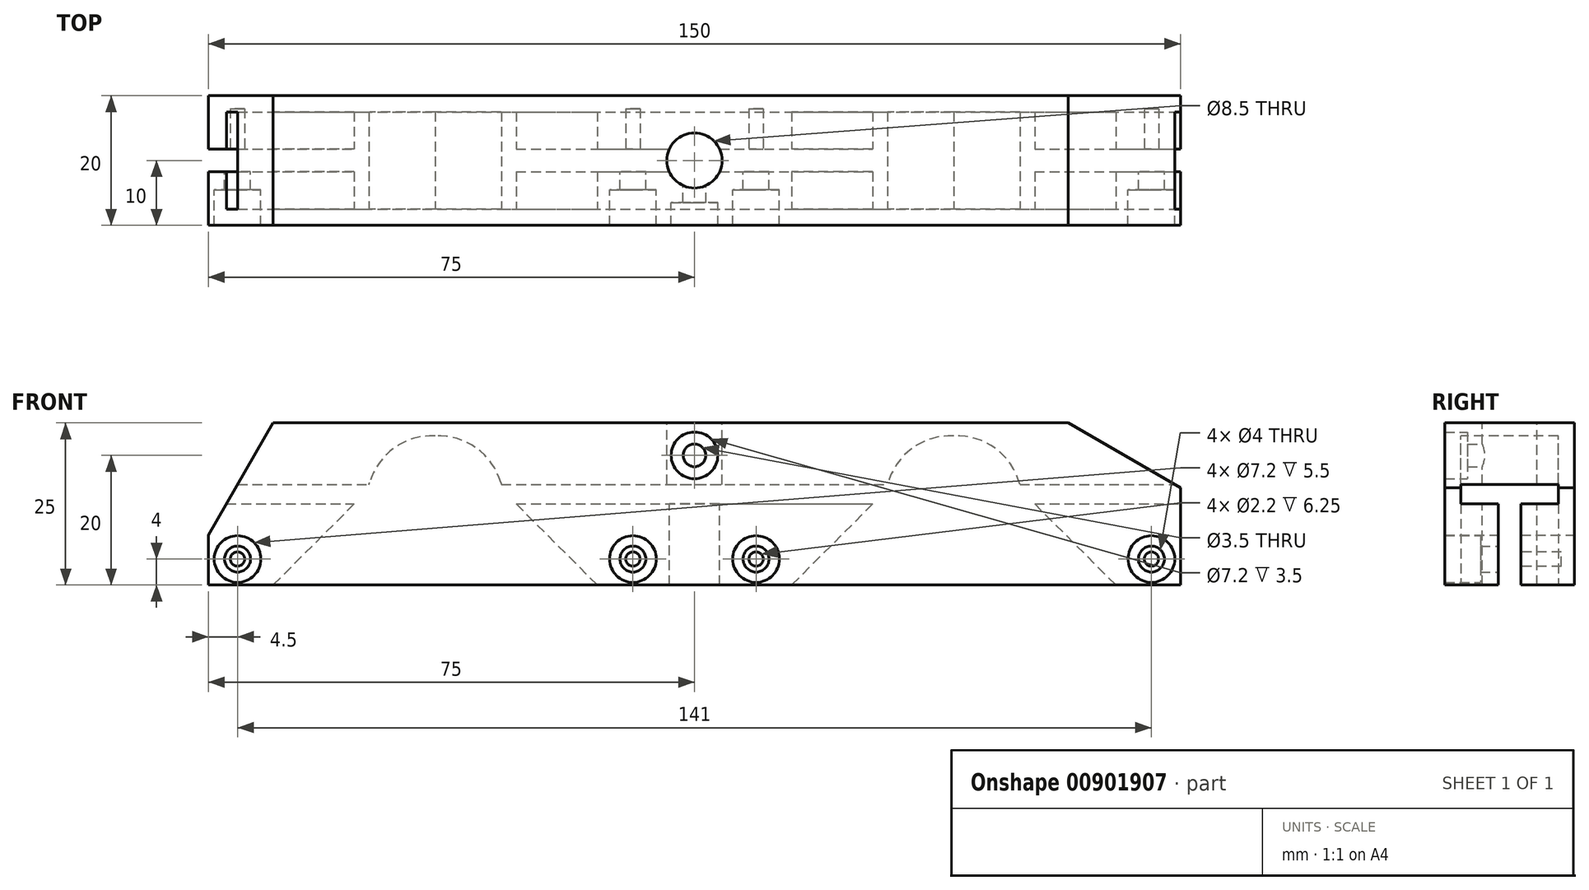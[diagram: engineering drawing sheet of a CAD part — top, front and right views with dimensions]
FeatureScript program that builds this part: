
annotation { "Feature Type Name" : "Feature", "Feature Type Description" : "" }
export const myFeature = defineFeature(function(context is Context, id is Id, definition is map)
    precondition{}
    {
        {
            var Q0;
            Q0=qCreatedBy(makeId("Front.planeOp"),FACE);
            var sketch = newSketch(context, id + "F0", { "sketchPlane" : qUnion([Q0])});
            skLineSegment(sketch, "E0.bottom", {"start": v(-75, 12.5) * mm, "end": v(75, 12.5) * mm});
            skLineSegment(sketch, "E0.top", {"start": v(-75, -12.5) * mm, "end": v(75, -12.5) * mm});
            skLineSegment(sketch, "E1", {"start": v(-50.5, -12.5) * mm, "end": v(-75, -12.5) * mm});
            skPoint(sketch, "E2.orphan", {"position": v(-50, 12.5) * mm});
            skPoint(sketch, "E3.orphan", {"position": v(50, 12.5) * mm});
            skLineSegment(sketch, "E4", {"start": v(-75, 12.5) * mm, "end": v(-75, -12.5) * mm});
            skLineSegment(sketch, "E5", {"start": v(75, 12.5) * mm, "end": v(75, -12.5) * mm});
            skSolve(sketch);
        }
        {
            var Q0;
            Q0=makeQuery(id+"F0.imprint","IMPRINT",FACE,{"disambiguationData":[TD([[makeQuery(id+"F0.imprint","IMPRINT",EDGE,{"derivedFrom":sQuery(id+"F0.wireOp",EDGE,"E0.bottom")}),-1.0]])]});
            extrude(context, id + "F1", {"entities" : qUnion([Q0]), "oppositeDirection" : true, "depth" : 10 * mm, "offsetDistance" : 25 * mm});
        }
        {
            var Q0;
            Q0=makeQuery(id+"F0.imprint","IMPRINT",FACE,{"disambiguationData":[TD([[makeQuery(id+"F0.imprint","IMPRINT",EDGE,{"derivedFrom":sQuery(id+"F0.wireOp",EDGE,"E0.bottom")}),-1.0]])]});
            var sketch = newSketch(context, id + "F2", { "sketchPlane" : qUnion([Q0])});
            skLineSegment(sketch, "E6", {"start": v(-40, 24.55) * mm, "end": v(-40, -25.43) * mm, "construction": true});
            skLineSegment(sketch, "E7", {"start": v(40, 21.57) * mm, "end": v(40, -24.69) * mm, "construction": true});
            skLineSegment(sketch, "E8", {"start": v(-41.62, 10.5) * mm, "end": v(42.45, 10.5) * mm, "construction": true});
            skLineSegment(sketch, "E9", {"start": v(-59.41, -12.5) * mm, "end": v(19.88, -12.5) * mm});
            skArc(sketch, "E10", {"start": v(-40, 10.5) * mm, "mid": v(-47.58, 7.58) * mm, "end": v(-50.5, 0) * mm});
            skArc(sketch, "E11", {"start": v(-29.5, 0) * mm, "mid": v(-32.42, 7.58) * mm, "end": v(-40, 10.5) * mm});
            skLineSegment(sketch, "E12", {"start": v(-50.5, 0) * mm, "end": v(-50.5, -12.5) * mm});
            skLineSegment(sketch, "E13", {"start": v(-29.5, 0) * mm, "end": v(-29.5, -12.5) * mm});
            skLineSegment(sketch, "E14", {"start": v(-29.5, 0) * mm, "end": v(17, 0) * mm});
            skArc(sketch, "E15", {"start": v(40, 10.5) * mm, "mid": v(32.42, 7.58) * mm, "end": v(29.5, 0) * mm});
            skArc(sketch, "E16", {"start": v(50.5, 0) * mm, "mid": v(47.58, 7.58) * mm, "end": v(40, 10.5) * mm});
            skLineSegment(sketch, "E17", {"start": v(17, -12.5) * mm, "end": v(62.5, -12.5) * mm});
            skLineSegment(sketch, "E18", {"start": v(17, 0) * mm, "end": v(29.5, 0) * mm});
            skLineSegment(sketch, "E19", {"start": v(62.5, -10.83) * mm, "end": v(62.5, -12.5) * mm});
            skLineSegment(sketch, "E20", {"start": v(50.5, 0) * mm, "end": v(52.5, 0) * mm});
            skLineSegment(sketch, "E21", {"start": v(62.5, -10) * mm, "end": v(62.5, -10.83) * mm});
            skLineSegment(sketch, "E22", {"start": v(29.5, 0) * mm, "end": v(29.5, -12.5) * mm});
            skLineSegment(sketch, "E23", {"start": v(50.5, 0) * mm, "end": v(50.5, -12.5) * mm});
            skPoint(sketch, "E24.orphan", {"position": v(-13.91, 0) * mm});
            skPoint(sketch, "E25.orphan", {"position": v(-13.91, -12.5) * mm});
            skLineSegment(sketch, "E26", {"start": v(-50.38, 2.12) * mm, "end": v(-65, -12.5) * mm});
            skLineSegment(sketch, "E27", {"start": v(-38, 10.5) * mm, "end": v(-37.88, 10.38) * mm});
            skPoint(sketch, "E28.orphan", {"position": v(-40, 12.5) * mm});
            skLineSegment(sketch, "E29.trimOffspring", {"start": v(-29.62, 2.12) * mm, "end": v(-15, -12.5) * mm});
            skPoint(sketch, "E30.orphan", {"position": v(-62.5, 0) * mm});
            skPoint(sketch, "E31.start.orphan", {"position": v(-62.5, -12) * mm});
            skLineSegment(sketch, "E32", {"start": v(38, 10.5) * mm, "end": v(37.88, 10.38) * mm});
            skLineSegment(sketch, "E33", {"start": v(42, 10.5) * mm, "end": v(42.12, 10.38) * mm});
            skPoint(sketch, "E34.orphan", {"position": v(40, 12.5) * mm});
            skLineSegment(sketch, "E35.trimOffspring", {"start": v(29.62, 2.12) * mm, "end": v(15, -12.5) * mm});
            skLineSegment(sketch, "E36.trimOffspring", {"start": v(50.38, 2.12) * mm, "end": v(65, -12.5) * mm});
            skPoint(sketch, "E37.orphan", {"position": v(62.5, 0) * mm});
            skSolve(sketch);
        }
        {
            var Q0;
            Q0=makeQuery(id+"F2.imprint","IMPRINT",FACE,{"disambiguationData":[TD([[makeQuery(id+"F2.imprint","IMPRINT",EDGE,{"derivedFrom":sQuery(id+"F2.wireOp",EDGE,"E10")}),1.0]])]});
            var Q1;
            Q1=makeQuery(id+"F2.imprint","IMPRINT",FACE,{"disambiguationData":[TD([[makeQuery(id+"F2.imprint","IMPRINT",EDGE,{"derivedFrom":sQuery(id+"F2.wireOp",EDGE,"E15")}),1.0]])]});
            var Q2;
            {var subQ0=sQuery(id+"F2.wireOp",EDGE,"E12");Q2=makeQuery(id+"F2.imprint","IMPRINT",FACE,{"disambiguationData":[TD([[makeQuery(id+"F2.imprint","IMPRINT",EDGE,{"derivedFrom":subQ0}),-1.0]])]});}
            var Q3;
            {var subQ0=sQuery(id+"F2.wireOp",EDGE,"E13");Q3=makeQuery(id+"F2.imprint","IMPRINT",FACE,{"disambiguationData":[TD([[makeQuery(id+"F2.imprint","IMPRINT",EDGE,{"derivedFrom":subQ0}),1.0]])]});}
            var Q4;
            {var subQ1=sQuery(id+"F2.wireOp",EDGE,"E11");var subQ3=sQuery(id+"F2.wireOp",EDGE,"E29.trimOffspring");var subQ4=makeQuery(id+"F2.imprint","INTERSECT",VERTEX,{"derivedFrom":[subQ1,subQ3]});Q4=makeQuery(id+"F2.imprint","IMPRINT",FACE,{"disambiguationData":[TD([[makeQuery(id+"F2.imprint","IMPRINT",EDGE,{"disambiguationData":[TD([[subQ4,-1.0]])],"derivedFrom":subQ3}),-1.0]])]});}
            var Q5;
            {var subQ0=sQuery(id+"F2.wireOp",EDGE,"E22");Q5=makeQuery(id+"F2.imprint","IMPRINT",FACE,{"disambiguationData":[TD([[makeQuery(id+"F2.imprint","IMPRINT",EDGE,{"derivedFrom":subQ0}),-1.0]])]});}
            var Q6;
            {var subQ1=sQuery(id+"F2.wireOp",EDGE,"E15");var subQ3=sQuery(id+"F2.wireOp",EDGE,"E35.trimOffspring");var subQ4=makeQuery(id+"F2.imprint","INTERSECT",VERTEX,{"derivedFrom":[subQ1,subQ3]});Q6=makeQuery(id+"F2.imprint","IMPRINT",FACE,{"disambiguationData":[TD([[makeQuery(id+"F2.imprint","IMPRINT",EDGE,{"disambiguationData":[TD([[subQ4,-1.0]])],"derivedFrom":subQ3}),1.0]])]});}
            var Q7;
            {var subQ0=sQuery(id+"F2.wireOp",EDGE,"E20");Q7=makeQuery(id+"F2.imprint","IMPRINT",FACE,{"disambiguationData":[TD([[makeQuery(id+"F2.imprint","IMPRINT",EDGE,{"derivedFrom":subQ0}),1.0]])]});}
            var Q8;
            {var subQ1=sQuery(id+"F2.wireOp",EDGE,"E19");Q8=makeQuery(id+"F2.imprint","IMPRINT",FACE,{"disambiguationData":[TD([[makeQuery(id+"F2.imprint","IMPRINT",EDGE,{"derivedFrom":subQ1}),-1.0]])]});}
            var Q9;
            {var subQ0=sQuery(id+"F2.wireOp",EDGE,"E19");Q9=makeQuery(id+"F2.imprint","IMPRINT",FACE,{"disambiguationData":[TD([[makeQuery(id+"F2.imprint","IMPRINT",EDGE,{"derivedFrom":subQ0}),1.0]])]});}
            extrude(context, id + "F3", {"entities" : qUnion([Q0, Q1, Q2, Q3, Q4, Q5, Q6, Q7, Q8, Q9]), "operationType" : NewBodyOperationType.REMOVE, "oppositeDirection" : true, "depth" : 7.5 * mm, "offsetDistance" : 25 * mm});
        }
        {
            var Q0;
            Q0=makeQuery(id+"F1.opExtrude","SWEPT_BODY",BODY,{"disambiguationData":[OSD([sQuery(id+"F0.wireOp",EDGE,"E0.bottom"),sQuery(id+"F0.wireOp",EDGE,"E0.top"),sQuery(id+"F0.wireOp",EDGE,"E4"),sQuery(id+"F0.wireOp",EDGE,"E5")])]});
            var Q1;
            Q1=makeQuery(id+"F0.imprint","IMPRINT",FACE,{"disambiguationData":[TD([[makeQuery(id+"F0.imprint","IMPRINT",EDGE,{"derivedFrom":sQuery(id+"F0.wireOp",EDGE,"E0.bottom")}),-1.0]])]});
            mirror(context, id + "F4", {"operationType" : NewBodyOperationType.ADD, "entities" : qUnion([Q0]), "mirrorPlane" : qUnion([Q1])});
        }
        {
            var Q0;
            {var subQ0=makeQuery(id+"F1.opExtrude","SWEPT_FACE",FACE,{"disambiguationData":[OSD([sQuery(id+"F0.wireOp",EDGE,"E0.bottom")])]});Q0=makeQuery(id+"F4.boolean.opBoolean","MERGE",FACE,{"derivedFrom":[subQ0,makeQuery(id+"F4.opPattern","COPY",FACE,{"derivedFrom":subQ0,"instanceName":"1"})]});}
            var sketch = newSketch(context, id + "F5", { "sketchPlane" : qUnion([Q0])});
            skCircle(sketch, "E38", {"center": v(0, 0) * mm, "radius": 4.25 * mm});
            skSolve(sketch);
        }
        {
            var Q0;
            Q0=makeQuery(id+"F5.imprint","IMPRINT",FACE,{"disambiguationData":[TD([[makeQuery(id+"F5.imprint","IMPRINT",EDGE,{"derivedFrom":sQuery(id+"F5.wireOp",EDGE,"E38")}),1.0]])]});
            extrude(context, id + "F6", {"entities" : qUnion([Q0]), "operationType" : NewBodyOperationType.REMOVE, "oppositeDirection" : true, "depth" : 30 * mm, "offsetDistance" : 25 * mm});
        }
        {
            var Q0;
            Q0=makeQuery(id+"F4.opPattern","COPY",FACE,{"derivedFrom":makeQuery(id+"F1.opExtrude","CAP_FACE",FACE,{"disambiguationData":[OSD([sQuery(id+"F0.wireOp",EDGE,"E0.bottom"),sQuery(id+"F0.wireOp",EDGE,"E0.top"),sQuery(id+"F0.wireOp",EDGE,"E4"),sQuery(id+"F0.wireOp",EDGE,"E5")])],"isStart":false}),"instanceName":"1"});
            var sketch = newSketch(context, id + "F7", { "sketchPlane" : qUnion([Q0])});
            skPoint(sketch, "E39", {"position": v(-70.5, -8.5) * mm});
            skPoint(sketch, "E40", {"position": v(-9.5, -8.5) * mm});
            skPoint(sketch, "E41", {"position": v(9.5, -8.5) * mm});
            skPoint(sketch, "E42", {"position": v(70.5, -8.5) * mm});
            skPoint(sketch, "E43", {"position": v(0, 7.5) * mm});
            skCircle(sketch, "E44", {"center": v(-70.5, -8.5) * mm, "radius": 1.1 * mm});
            skCircle(sketch, "E45", {"center": v(-9.5, -8.5) * mm, "radius": 1.1 * mm});
            skCircle(sketch, "E46", {"center": v(9.5, -8.5) * mm, "radius": 1.1 * mm});
            skCircle(sketch, "E47", {"center": v(70.5, -8.5) * mm, "radius": 1.1 * mm});
            skSolve(sketch);
        }
        {
            var Q0;
            Q0=sQuery(id+"F7.wireOp",VERTEX,"E39");
            var Q1;
            Q1=sQuery(id+"F7.wireOp",VERTEX,"E40");
            var Q2;
            Q2=sQuery(id+"F7.wireOp",VERTEX,"E41");
            var Q3;
            Q3=sQuery(id+"F7.wireOp",VERTEX,"E42");
            var Q4;
            Q4=makeQuery(id+"F1.opExtrude","SWEPT_BODY",BODY,{"disambiguationData":[OSD([sQuery(id+"F0.wireOp",EDGE,"E0.bottom"),sQuery(id+"F0.wireOp",EDGE,"E0.top"),sQuery(id+"F0.wireOp",EDGE,"E4"),sQuery(id+"F0.wireOp",EDGE,"E5")])]});
            hole(context, id + "F8", {"style" : HoleStyle.C_BORE, "endStyle" : HoleEndStyle.BLIND, "holeDiameter" : 4 * mm, "cBoreDiameter" : 7.2 * mm, "cBoreDepth" : 5.5 * mm, "majorDiameter" : 5 * mm, "holeDepth" : 8.5 * mm, "isTappedThrough" : true, "tappedDepth" : 12 * mm, "tapClearance" : 3, "locations" : qUnion([Q0, Q1, Q2, Q3]), "scope" : qUnion([Q4]), "startStyle" : HoleStartStyle.SKETCH});
        }
        {
            var Q0;
            Q0=sQuery(id+"F7.wireOp",VERTEX,"E43");
            var Q1;
            Q1=makeQuery(id+"F1.opExtrude","SWEPT_BODY",BODY,{"disambiguationData":[OSD([sQuery(id+"F0.wireOp",EDGE,"E0.bottom"),sQuery(id+"F0.wireOp",EDGE,"E0.top"),sQuery(id+"F0.wireOp",EDGE,"E4"),sQuery(id+"F0.wireOp",EDGE,"E5")])]});
            hole(context, id + "F9", {"style" : HoleStyle.C_BORE, "endStyle" : HoleEndStyle.BLIND, "holeDiameter" : 3.5 * mm, "cBoreDiameter" : 7.2 * mm, "cBoreDepth" : 3.5 * mm, "majorDiameter" : 5 * mm, "holeDepth" : 7 * mm, "isTappedThrough" : true, "tappedDepth" : 12 * mm, "tapClearance" : 3, "locations" : qUnion([Q0]), "scope" : qUnion([Q1]), "startStyle" : HoleStartStyle.SKETCH});
        }
        {
            var Q0;
            Q0=makeQuery(id+"F3.boolean.opBoolean","COPY",EDGE,{"derivedFrom":makeQuery(id+"F3.opExtrude","SWEPT_EDGE",EDGE,{"disambiguationData":[OSD([sQuery(id+"F2.wireOp",EDGE,"E11"),sQuery(id+"F2.wireOp",EDGE,"E29.trimOffspring")])]})});
            fillet(context, id + "F10", {"entities" : qUnion([Q0]), "radius" : 5 * mm, "tangentPropagation" : true, "allowEdgeOverflow" : false});
        }
        {
            var Q0;
            Q0=makeQuery(id+"F3.boolean.opBoolean","COPY",EDGE,{"derivedFrom":makeQuery(id+"F3.opExtrude","SWEPT_EDGE",EDGE,{"disambiguationData":[OSD([sQuery(id+"F2.wireOp",EDGE,"E10"),sQuery(id+"F2.wireOp",EDGE,"E26")])]})});
            fillet(context, id + "F11", {"entities" : qUnion([Q0]), "radius" : 5 * mm, "tangentPropagation" : true, "allowEdgeOverflow" : false});
        }
        {
            var Q0;
            {var subQ0=makeQuery(id+"F1.opExtrude","SWEPT_FACE",FACE,{"disambiguationData":[OSD([sQuery(id+"F0.wireOp",EDGE,"E5")])]});Q0=makeQuery(id+"F4.boolean.opBoolean","MERGE",FACE,{"derivedFrom":[subQ0,makeQuery(id+"F4.opPattern","COPY",FACE,{"derivedFrom":subQ0,"instanceName":"1"})]});}
            var sketch = newSketch(context, id + "F12", { "sketchPlane" : qUnion([Q0])});
            skLineSegment(sketch, "E48.bottom", {"start": v(-1.75, -12.5) * mm, "end": v(1.75, -12.5) * mm});
            skLineSegment(sketch, "E48.top", {"start": v(-1.75, 0) * mm, "end": v(1.75, 0) * mm});
            skLineSegment(sketch, "E48.left", {"start": v(-1.75, -12.5) * mm, "end": v(-1.75, 0) * mm});
            skLineSegment(sketch, "E48.right", {"start": v(1.75, -12.5) * mm, "end": v(1.75, 0) * mm});
            skLineSegment(sketch, "E49.bottom", {"start": v(-7.5, 0) * mm, "end": v(7.5, 0) * mm});
            skLineSegment(sketch, "E49.top", {"start": v(-7.5, 3) * mm, "end": v(7.5, 3) * mm});
            skLineSegment(sketch, "E49.left", {"start": v(-7.5, 0) * mm, "end": v(-7.5, 3) * mm});
            skLineSegment(sketch, "E49.right", {"start": v(7.5, 0) * mm, "end": v(7.5, 3) * mm});
            skPoint(sketch, "E50.end.orphan", {"position": v(-1.75, -9.96) * mm});
            skPoint(sketch, "E51.end.orphan", {"position": v(1.75, -9.96) * mm});
            skSolve(sketch);
        }
        {
            var Q0;
            Q0=makeQuery(id+"F12.imprint","IMPRINT",FACE,{"disambiguationData":[TD([[makeQuery(id+"F12.imprint","IMPRINT",EDGE,{"derivedFrom":sQuery(id+"F12.wireOp",EDGE,"E48.bottom")}),-1.0]])]});
            var Q1;
            {var subQ1=sQuery(id+"F12.wireOp",EDGE,"E48.top");Q1=makeQuery(id+"F12.imprint","IMPRINT",FACE,{"disambiguationData":[TD([[makeQuery(id+"F12.imprint","IMPRINT",EDGE,{"derivedFrom":subQ1}),1.0]])]});}
            extrude(context, id + "F13", {"entities" : qUnion([Q0, Q1]), "operationType" : NewBodyOperationType.REMOVE, "endBound" : BoundingType.THROUGH_ALL, "oppositeDirection" : true, "depth" : 25 * mm, "offsetDistance" : 25 * mm});
        }
        {
            var Q0;
            Q0=makeQuery(id+"F7.imprint","IMPRINT",FACE,{"disambiguationData":[TD([[makeQuery(id+"F7.imprint","IMPRINT",EDGE,{"derivedFrom":sQuery(id+"F7.wireOp",EDGE,"E44")}),1.0]])]});
            var Q1;
            Q1=makeQuery(id+"F7.imprint","IMPRINT",FACE,{"disambiguationData":[TD([[makeQuery(id+"F7.imprint","IMPRINT",EDGE,{"derivedFrom":sQuery(id+"F7.wireOp",EDGE,"E45")}),1.0]])]});
            var Q2;
            Q2=makeQuery(id+"F7.imprint","IMPRINT",FACE,{"disambiguationData":[TD([[makeQuery(id+"F7.imprint","IMPRINT",EDGE,{"derivedFrom":sQuery(id+"F7.wireOp",EDGE,"E46")}),1.0]])]});
            var Q3;
            Q3=makeQuery(id+"F7.imprint","IMPRINT",FACE,{"disambiguationData":[TD([[makeQuery(id+"F7.imprint","IMPRINT",EDGE,{"derivedFrom":sQuery(id+"F7.wireOp",EDGE,"E47")}),1.0]])]});
            extrude(context, id + "F14", {"entities" : qUnion([Q0, Q1, Q2, Q3]), "operationType" : NewBodyOperationType.REMOVE, "oppositeDirection" : true, "depth" : 18 * mm, "offsetDistance" : 25 * mm});
        }
        {
            var Q0;
            {var subQ0=makeQuery(id+"F1.opExtrude","SWEPT_EDGE",EDGE,{"disambiguationData":[OSD([sQuery(id+"F0.wireOp",EDGE,"E0.bottom"),sQuery(id+"F0.wireOp",EDGE,"E4")])]});Q0=makeQuery(id+"F4.boolean.opBoolean","MERGE",EDGE,{"derivedFrom":[subQ0,makeQuery(id+"F4.opPattern","COPY",EDGE,{"derivedFrom":subQ0,"instanceName":"1"})]});}
            chamfer(context, id + "F15", {"entities" : qUnion([Q0]), "chamferType" : ChamferType.OFFSET_ANGLE, "width" : 10 * mm, "oppositeDirection" : false, "angle" : 60 * degree, "tangentPropagation" : true});
        }
        {
            var Q0;
            {var subQ0=makeQuery(id+"F1.opExtrude","SWEPT_EDGE",EDGE,{"disambiguationData":[OSD([sQuery(id+"F0.wireOp",EDGE,"E0.bottom"),sQuery(id+"F0.wireOp",EDGE,"E5")])]});Q0=makeQuery(id+"F4.boolean.opBoolean","MERGE",EDGE,{"derivedFrom":[subQ0,makeQuery(id+"F4.opPattern","COPY",EDGE,{"derivedFrom":subQ0,"instanceName":"1"})]});}
            chamfer(context, id + "F16", {"entities" : qUnion([Q0]), "chamferType" : ChamferType.OFFSET_ANGLE, "width" : 10 * mm, "oppositeDirection" : true, "angle" : 60 * degree, "tangentPropagation" : true});
        }
    });
